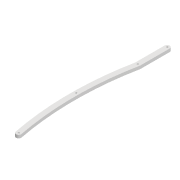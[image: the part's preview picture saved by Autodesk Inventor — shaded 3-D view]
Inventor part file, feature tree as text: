
AUTODESK INVENTOR PART (.ipt)
format: ipt  version: 2022 (Build 260153000, 153)  size: 102,912 bytes
history: native  units: mm
features: extrude x1
ambient origin geometry x8: Origin, YZ Plane, XZ Plane, XY Plane, X Axis, Y Axis, Z Axis, Center Point
bodies: Solid1 (feature_tree)
feature tree (1):
  extrude  "Extrusion1"  Depth=3.3mm
